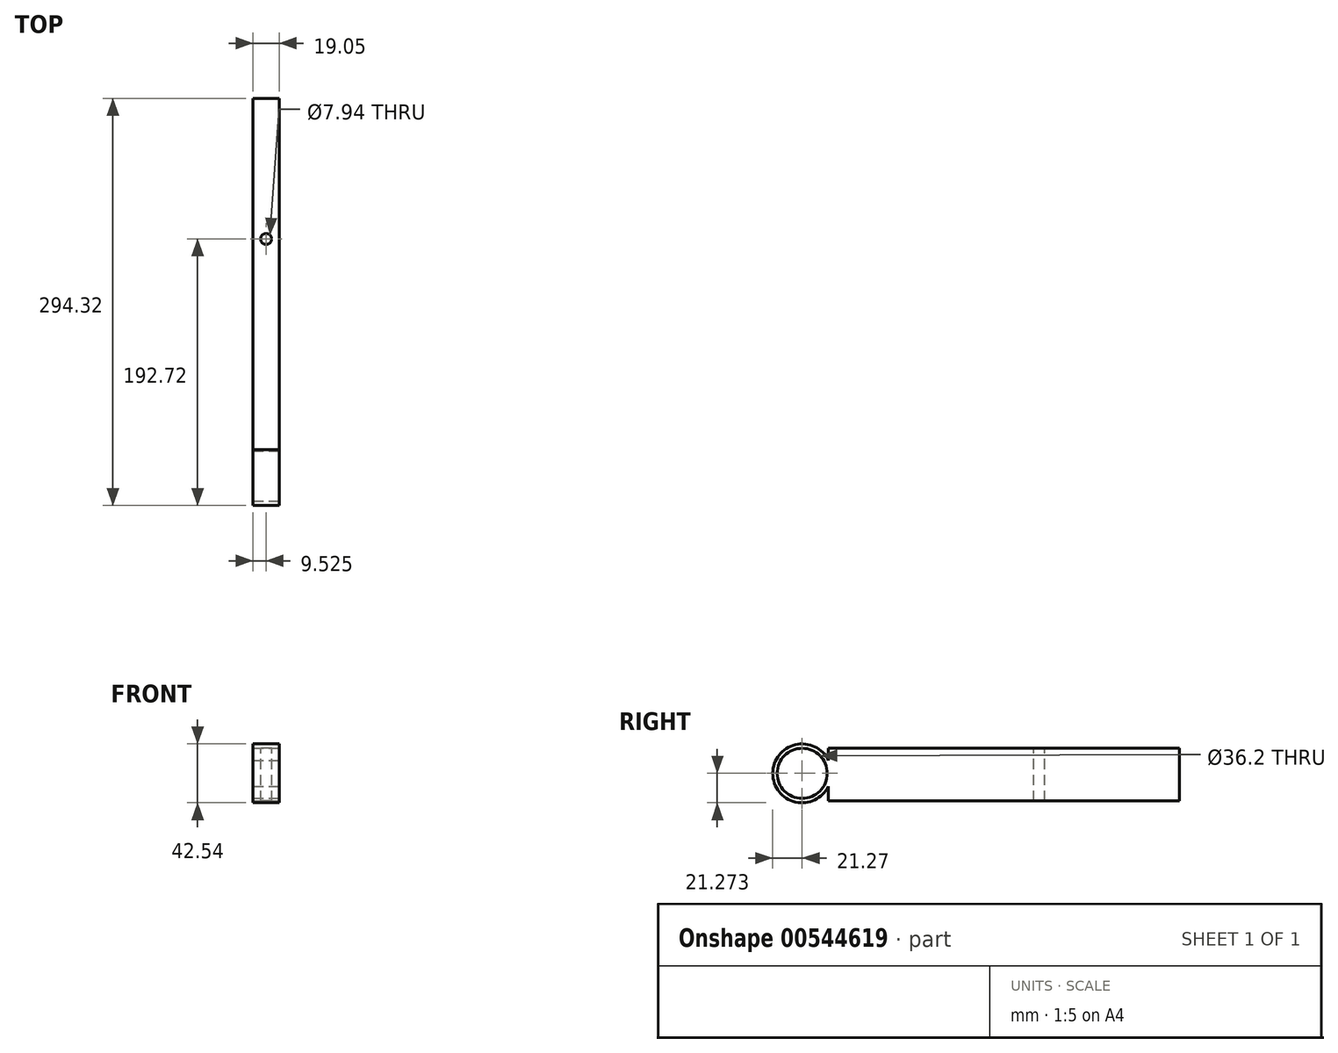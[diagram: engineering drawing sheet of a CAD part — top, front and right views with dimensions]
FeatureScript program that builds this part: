
annotation { "Feature Type Name" : "Feature", "Feature Type Description" : "" }
export const myFeature = defineFeature(function(context is Context, id is Id, definition is map)
    precondition{}
    {
        {
            var Q0;
            Q0=qCreatedBy(makeId("Front.planeOp"),FACE);
            var sketch = newSketch(context, id + "F0", { "sketchPlane" : qUnion([Q0])});
            skLineSegment(sketch, "E0.bottom", {"start": v(0, 0) * mm, "end": v(19.05, 0) * mm});
            skLineSegment(sketch, "E0.top", {"start": v(0, 38.1) * mm, "end": v(19.05, 38.1) * mm});
            skLineSegment(sketch, "E0.left", {"start": v(0, 0) * mm, "end": v(0, 38.1) * mm});
            skLineSegment(sketch, "E0.right", {"start": v(19.05, 0) * mm, "end": v(19.05, 38.1) * mm});
            skSolve(sketch);
        }
        {
            var Q0;
            Q0 = qSketchRegion(id + "F0", true);
            extrude(context, id + "F1", {"entities" : qUnion([Q0]), "endBound" : BoundingType.SYMMETRIC, "depth" : 254 * mm, "offsetDistance" : 25.4 * mm});
        }
        {
            var Q0;
            Q0=makeQuery(id+"F1.opExtrude","SWEPT_FACE",FACE,{"disambiguationData":[OSD([sQuery(id+"F0.wireOp",EDGE,"E0.right")])]});
            var sketch = newSketch(context, id + "F2", { "sketchPlane" : qUnion([Q0])});
            skCircle(sketch, "E1", {"center": v(-146.05, 20) * mm, "radius": 21.27 * mm});
            skCircle(sketch, "E2", {"center": v(-146.05, 20) * mm, "radius": 18.1 * mm});
            skSolve(sketch);
        }
        {
            var Q0;
            Q0=makeQuery(id+"F2.imprint","IMPRINT",FACE,{"disambiguationData":[TD([[makeQuery(id+"F2.imprint","IMPRINT",EDGE,{"derivedFrom":sQuery(id+"F2.wireOp",EDGE,"E2")}),-1.0]])]});
            extrude(context, id + "F3", {"entities" : qUnion([Q0]), "oppositeDirection" : true, "depth" : 19.05 * mm, "offsetDistance" : 25.4 * mm});
        }
        {
            var Q0;
            Q0=makeQuery(id+"F3.opExtrude","SWEPT_BODY",BODY,{"disambiguationData":[OSD([sQuery(id+"F0.wireOp",EDGE,"E0.right"),sQuery(id+"F2.wireOp",EDGE,"E1"),sQuery(id+"F2.wireOp",EDGE,"E2")])]});
            var Q1;
            Q1=makeQuery(id+"F1.opExtrude","SWEPT_BODY",BODY,{"disambiguationData":[OSD([sQuery(id+"F0.wireOp",EDGE,"E0.bottom"),sQuery(id+"F0.wireOp",EDGE,"E0.top"),sQuery(id+"F0.wireOp",EDGE,"E0.left"),sQuery(id+"F0.wireOp",EDGE,"E0.right")])]});
            booleanBodies(context, id + "F4", {"operationType" : BooleanOperationType.UNION, "tools" : qUnion([Q0, Q1])});
        }
        {
            var Q0;
            Q0=makeQuery(id+"F1.opExtrude","SWEPT_FACE",FACE,{"disambiguationData":[OSD([sQuery(id+"F0.wireOp",EDGE,"E0.top")])]});
            var sketch = newSketch(context, id + "F5", { "sketchPlane" : qUnion([Q0])});
            skCircle(sketch, "E3", {"center": v(9.53, 25.4) * mm, "radius": 3.97 * mm});
            skSolve(sketch);
        }
        {
            var Q0;
            Q0=makeQuery(id+"F5.imprint","IMPRINT",FACE,{"disambiguationData":[TD([[makeQuery(id+"F5.imprint","IMPRINT",EDGE,{"derivedFrom":sQuery(id+"F5.wireOp",EDGE,"E3")}),1.0]])]});
            extrude(context, id + "F6", {"entities" : qUnion([Q0]), "operationType" : NewBodyOperationType.REMOVE, "endBound" : BoundingType.THROUGH_ALL, "oppositeDirection" : true, "depth" : 25.4 * mm, "offsetDistance" : 25.4 * mm});
        }
    });
